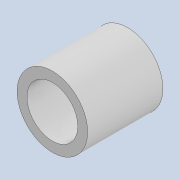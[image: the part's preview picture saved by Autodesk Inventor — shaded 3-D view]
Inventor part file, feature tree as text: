
AUTODESK INVENTOR PART (.ipt)
format: ipt  version: 2020 (Build 240168000, 168)  size: 112,128 bytes
history: native  units: mm
features: extrude x1, sketch x1
ambient origin geometry x8: Origin, YZ Plane, XZ Plane, XY Plane, X Axis, Y Axis, Z Axis, Center Point
bodies: Solid1 (feature_tree)
feature tree (2):
  extrude  "Extrusion1"  Depth=16.0mm
  sketch  "Sketch1"  dims[d0=15.0mm d1=10.8mm d2=16.0mm d3=0.0mm]
